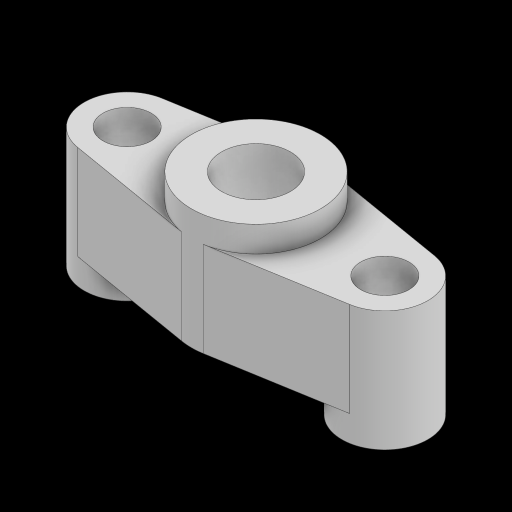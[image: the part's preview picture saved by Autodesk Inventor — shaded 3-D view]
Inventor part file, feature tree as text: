
AUTODESK INVENTOR PART (.ipt)
format: ipt  version: 2024 (Build 280153000, 153)  size: 167,936 bytes
history: native  units: mm
features: extrude x3, sketch x3, projected_geometry x3, plane x1
ambient origin geometry x8: Origin, YZ Plane, XZ Plane, XY Plane, X Axis, Y Axis, Z Axis, Center Point
bodies: Volumenkörper1 (feature_tree)
feature tree (10):
  extrude  "Extrusion1"  Depth=14.0mm TaperAngle=0.0deg
  plane  "Arbeitsebene1"
  extrude  "Extrusion2"  [1 undecoded]
  extrude  "Extrusion3"  Depth=10.0mm
  sketch  "Skizze1"  dims[d0=15.0mm d1=14.0mm d2=0.0mm]
  sketch  "Skizze2"  dims[d3=8.0mm d4=-3.0mm]
  sketch  "Skizze3"  dims[d5=10.0mm d6=10.0mm d7=15.0mm d8=15.0mm d9=5.6mm d10=5.6mm d11=14.0mm d12=0.0mm d13=11.0mm d14=0.0mm]
  projected_geometry  "Projizierte Kontur1"
  projected_geometry  "Projizierte Kontur2"
  projected_geometry  "Projizierte Kontur3"
note: 1 required parameter value undecoded (feature->parameter linkage not recoverable at this tier; creation-order binding heuristic only, values carry confidence <= 0.55)
